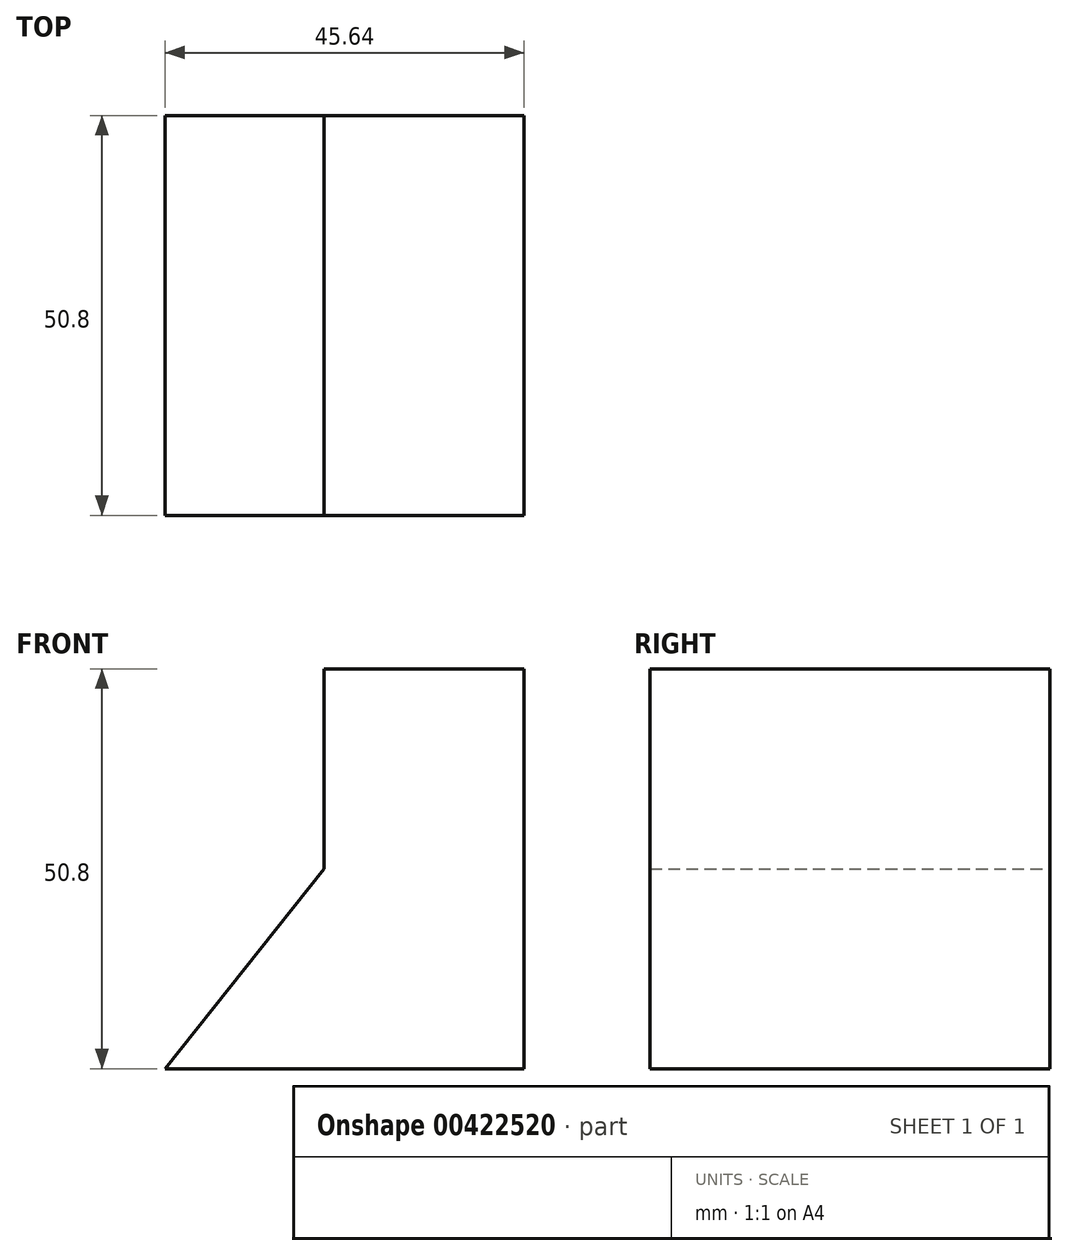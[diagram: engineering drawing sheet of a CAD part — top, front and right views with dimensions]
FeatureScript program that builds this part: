
annotation { "Feature Type Name" : "Feature", "Feature Type Description" : "" }
export const myFeature = defineFeature(function(context is Context, id is Id, definition is map)
    precondition{}
    {
        {
            var Q0;
            Q0=qCreatedBy(makeId("Front.planeOp"),FACE);
            var sketch = newSketch(context, id + "F0", { "sketchPlane" : qUnion([Q0])});
            skLineSegment(sketch, "E0", {"start": v(0, 0) * mm, "end": v(0, 50.8) * mm});
            skLineSegment(sketch, "E1", {"start": v(0, 50.8) * mm, "end": v(-25.4, 50.8) * mm});
            skLineSegment(sketch, "E2", {"start": v(-25.4, 50.8) * mm, "end": v(-25.4, 25.4) * mm});
            skLineSegment(sketch, "E3", {"start": v(-25.4, 25.4) * mm, "end": v(-41.23, 5.53) * mm});
            skLineSegment(sketch, "E4", {"start": v(0, 0) * mm, "end": v(-36.08, 0) * mm});
            skLineSegment(sketch, "E5", {"start": v(-3.3, 0) * mm, "end": v(-45.64, 0) * mm});
            skLineSegment(sketch, "E6", {"start": v(-45.64, 0) * mm, "end": v(-25.4, 25.4) * mm});
            skSolve(sketch);
        }
        {
            var Q0;
            Q0 = qSketchRegion(id + "F0", true);
            extrude(context, id + "F1", {"entities" : qUnion([Q0]), "depth" : 50.8 * mm});
        }
    });
